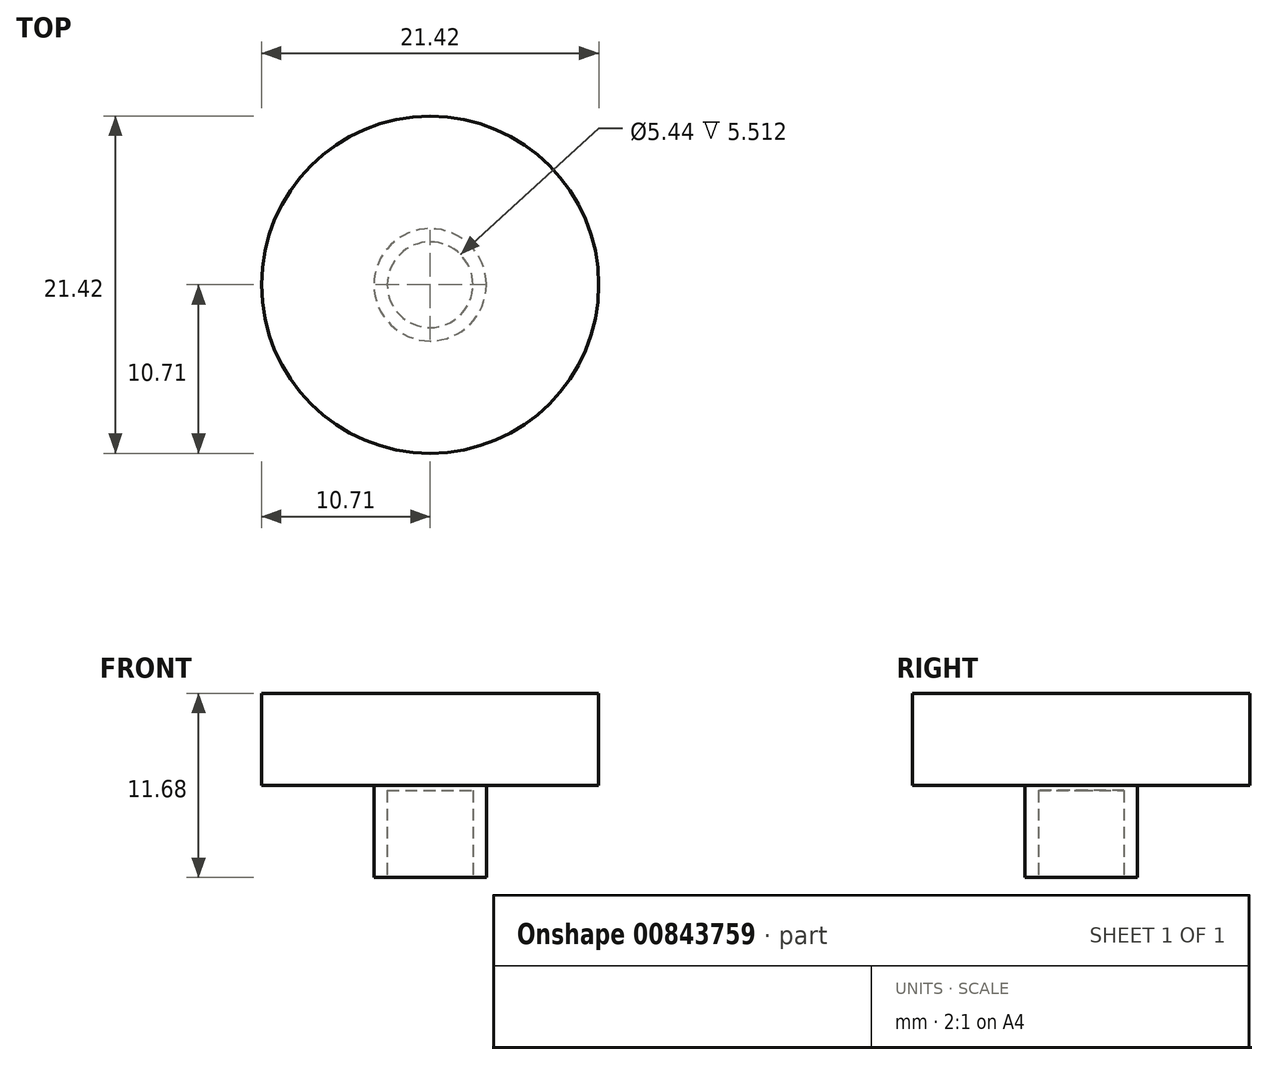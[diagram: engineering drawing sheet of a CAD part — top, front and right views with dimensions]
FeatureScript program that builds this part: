
annotation { "Feature Type Name" : "Feature", "Feature Type Description" : "" }
export const myFeature = defineFeature(function(context is Context, id is Id, definition is map)
    precondition{}
    {
        {
            var Q0;
            Q0=qCreatedBy(makeId("Top.planeOp"),FACE);
            var sketch = newSketch(context, id + "F0", { "sketchPlane" : qUnion([Q0])});
            skCircle(sketch, "E0", {"center": v(0, 0) * mm, "radius": 10.7 * mm});
            skSolve(sketch);
        }
        {
            var Q0;
            Q0=makeQuery(id+"F0.imprint","IMPRINT",FACE,{"disambiguationData":[TD([[makeQuery(id+"F0.imprint","IMPRINT",EDGE,{"derivedFrom":sQuery(id+"F0.wireOp",EDGE,"E0")}),1.0]])]});
            extrude(context, id + "F1", {"entities" : qUnion([Q0]), "depth" : 5.84 * mm, "offsetDistance" : 25.4 * mm});
        }
        {
            var Q0;
            Q0=makeQuery(id+"F1.opExtrude","CAP_FACE",FACE,{"disambiguationData":[OSD([sQuery(id+"F0.wireOp",EDGE,"E0")])],"isStart":true});
            var sketch = newSketch(context, id + "F2", { "sketchPlane" : qUnion([Q0])});
            skCircle(sketch, "E1", {"center": v(0, 0) * mm, "radius": 3.57 * mm});
            skSolve(sketch);
        }
        {
            var Q0;
            Q0=makeQuery(id+"F2.imprint","IMPRINT",FACE,{"disambiguationData":[TD([[makeQuery(id+"F2.imprint","IMPRINT",EDGE,{"derivedFrom":sQuery(id+"F2.wireOp",EDGE,"E1")}),1.0]])]});
            extrude(context, id + "F3", {"entities" : qUnion([Q0]), "operationType" : NewBodyOperationType.ADD, "depth" : 5.84 * mm, "offsetDistance" : 25.4 * mm});
        }
        {
            var Q0;
            Q0=makeQuery(id+"F3.opExtrude","CAP_FACE",FACE,{"disambiguationData":[OSD([sQuery(id+"F2.wireOp",EDGE,"E1")])],"isStart":false});
            var sketch = newSketch(context, id + "F4", { "sketchPlane" : qUnion([Q0])});
            skCircle(sketch, "E2", {"center": v(0, 0) * mm, "radius": 2.72 * mm});
            skSolve(sketch);
        }
        {
            var Q0;
            Q0=makeQuery(id+"F4.imprint","IMPRINT",FACE,{"disambiguationData":[TD([[makeQuery(id+"F4.imprint","IMPRINT",EDGE,{"derivedFrom":sQuery(id+"F4.wireOp",EDGE,"E2")}),1.0]])]});
            extrude(context, id + "F5", {"entities" : qUnion([Q0]), "operationType" : NewBodyOperationType.ADD, "oppositeDirection" : true, "depth" : 5.5 * mm, "offsetDistance" : 25.4 * mm});
        }
        {
            var Q0;
            Q0=makeQuery(id+"F3.opExtrude","CAP_FACE",FACE,{"disambiguationData":[OSD([sQuery(id+"F2.wireOp",EDGE,"E1")])],"isStart":false});
            var sketch = newSketch(context, id + "F6", { "sketchPlane" : qUnion([Q0])});
            skCircle(sketch, "E3", {"center": v(0, 0) * mm, "radius": 2.72 * mm});
            skSolve(sketch);
        }
        {
            var Q0;
            Q0=makeQuery(id+"F6.imprint","IMPRINT",FACE,{"disambiguationData":[TD([[makeQuery(id+"F6.imprint","IMPRINT",EDGE,{"derivedFrom":sQuery(id+"F6.wireOp",EDGE,"E3")}),1.0]])]});
            extrude(context, id + "F7", {"entities" : qUnion([Q0]), "operationType" : NewBodyOperationType.ADD, "oppositeDirection" : true, "depth" : 5.5 * mm, "offsetDistance" : 25.4 * mm});
        }
        {
            var Q0;
            Q0=makeQuery(id+"F3.opExtrude","CAP_FACE",FACE,{"disambiguationData":[OSD([sQuery(id+"F2.wireOp",EDGE,"E1")])],"isStart":false});
            var sketch = newSketch(context, id + "F8", { "sketchPlane" : qUnion([Q0])});
            skCircle(sketch, "E4", {"center": v(0, 0) * mm, "radius": 2.72 * mm});
            skSolve(sketch);
        }
        {
            var Q0;
            Q0=makeQuery(id+"F8.imprint","IMPRINT",FACE,{"disambiguationData":[TD([[makeQuery(id+"F8.imprint","IMPRINT",EDGE,{"derivedFrom":sQuery(id+"F8.wireOp",EDGE,"E4")}),1.0]])]});
            extrude(context, id + "F9", {"entities" : qUnion([Q0]), "operationType" : NewBodyOperationType.REMOVE, "oppositeDirection" : true, "depth" : 5.5 * mm, "offsetDistance" : 25.4 * mm});
        }
    });
